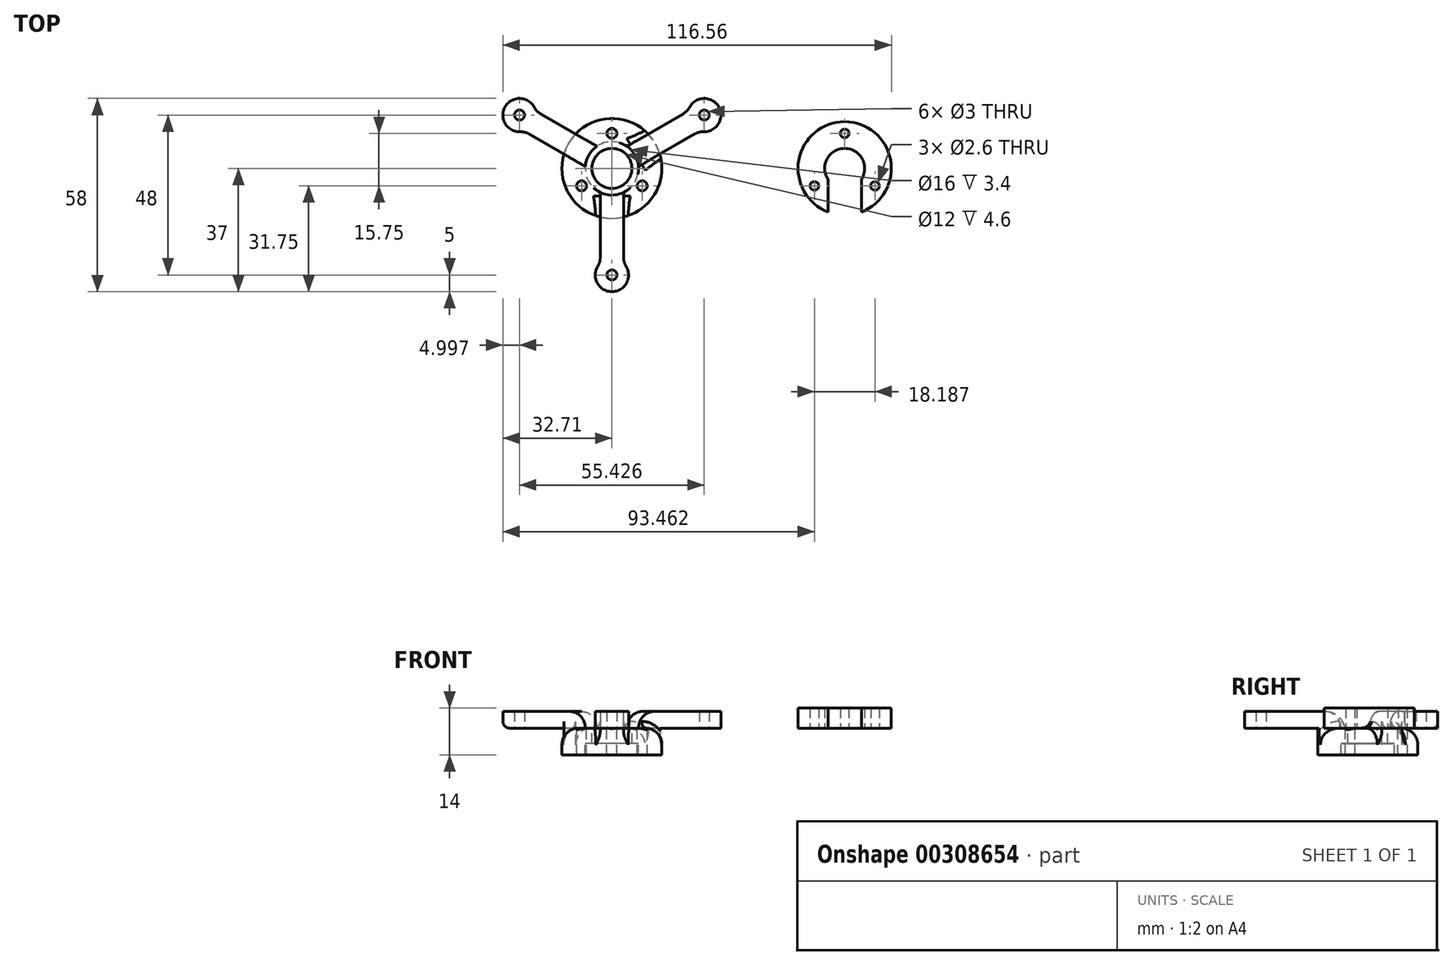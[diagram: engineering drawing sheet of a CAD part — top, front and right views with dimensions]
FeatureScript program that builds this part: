
annotation { "Feature Type Name" : "Feature", "Feature Type Description" : "" }
export const myFeature = defineFeature(function(context is Context, id is Id, definition is map)
    precondition{}
    {
        {
            var Q0;
            Q0=qCreatedBy(makeId("Top.planeOp"),FACE);
            var sketch = newSketch(context, id + "F0", { "sketchPlane" : qUnion([Q0])});
            skCircle(sketch, "E0", {"center": v(0, 0) * mm, "radius": 32 * mm});
            skLineSegment(sketch, "E1", {"start": v(5.2, 3) * mm, "end": v(27.71, 16) * mm});
            skCircle(sketch, "E2", {"center": v(27.71, 16) * mm, "radius": 1.5 * mm});
            skCircle(sketch, "E3", {"center": v(27.71, 16) * mm, "radius": 5 * mm});
            skLineSegment(sketch, "E4", {"start": v(25.11, 14.5) * mm, "end": v(23.36, 17.53) * mm});
            skLineSegment(sketch, "E5", {"start": v(23.36, 17.53) * mm, "end": v(20.33, 15.78) * mm});
            skLineSegment(sketch, "E6", {"start": v(20.33, 15.78) * mm, "end": v(22.08, 12.75) * mm});
            skLineSegment(sketch, "E7.MirrorCS", {"start": v(26.86, 11.47) * mm, "end": v(23.83, 9.72) * mm});
            skLineSegment(sketch, "E8.MirrorCS", {"start": v(23.83, 9.72) * mm, "end": v(22.08, 12.75) * mm});
            skLineSegment(sketch, "E9.MirrorCS", {"start": v(25.11, 14.5) * mm, "end": v(26.86, 11.47) * mm});
            skCircle(sketch, "E10.1.0", {"center": v(-27.71, 16) * mm, "radius": 5 * mm});
            skCircle(sketch, "E10.1.1", {"center": v(-27.71, 16) * mm, "radius": 1.5 * mm});
            skLineSegment(sketch, "E10.1.2", {"start": v(-25.11, 14.5) * mm, "end": v(-26.86, 11.47) * mm});
            skLineSegment(sketch, "E10.1.3", {"start": v(-25.11, 14.5) * mm, "end": v(-23.36, 17.53) * mm});
            skLineSegment(sketch, "E10.1.4", {"start": v(-23.36, 17.53) * mm, "end": v(-20.33, 15.78) * mm});
            skLineSegment(sketch, "E10.1.5", {"start": v(-20.33, 15.78) * mm, "end": v(-22.08, 12.75) * mm});
            skLineSegment(sketch, "E10.1.6", {"start": v(-23.83, 9.72) * mm, "end": v(-22.08, 12.75) * mm});
            skLineSegment(sketch, "E10.1.7", {"start": v(-26.86, 11.47) * mm, "end": v(-23.83, 9.72) * mm});
            skCircle(sketch, "E10.2.0", {"center": v(0, -32) * mm, "radius": 5 * mm});
            skCircle(sketch, "E10.2.1", {"center": v(0, -32) * mm, "radius": 1.5 * mm});
            skLineSegment(sketch, "E10.2.2", {"start": v(0, -29) * mm, "end": v(3.5, -29) * mm});
            skLineSegment(sketch, "E10.2.3", {"start": v(0, -29) * mm, "end": v(-3.5, -29) * mm});
            skLineSegment(sketch, "E10.2.4", {"start": v(-3.5, -29) * mm, "end": v(-3.5, -25.5) * mm});
            skLineSegment(sketch, "E10.2.5", {"start": v(-3.5, -25.5) * mm, "end": v(0, -25.5) * mm});
            skLineSegment(sketch, "E10.2.6", {"start": v(3.5, -25.5) * mm, "end": v(0, -25.5) * mm});
            skLineSegment(sketch, "E10.2.7", {"start": v(3.5, -29) * mm, "end": v(3.5, -25.5) * mm});
            skLineSegment(sketch, "E11.0", {"start": v(5.97, -0.6) * mm, "end": v(29.3, 12.87) * mm});
            skLineSegment(sketch, "E12.0", {"start": v(2.47, 5.47) * mm, "end": v(25.8, 18.94) * mm});
            skCircle(sketch, "E13", {"center": v(0, 0) * mm, "radius": 6 * mm});
            skCircle(sketch, "E14", {"center": v(0, 0) * mm, "radius": 8 * mm});
            skCircle(sketch, "E15", {"center": v(0, 0) * mm, "radius": 15 * mm});
            skLineSegment(sketch, "E16", {"start": v(-32.04, 13.5) * mm, "end": v(-4.33, -34.5) * mm});
            skLineSegment(sketch, "E17", {"start": v(-18.19, -10.5) * mm, "end": v(-16.45, -9.5) * mm});
            skCircle(sketch, "E18", {"center": v(0, 0) * mm, "radius": 25 * mm});
            skCircle(sketch, "E19", {"center": v(0, 10.5) * mm, "radius": 1.5 * mm});
            skCircle(sketch, "E20.1.0", {"center": v(-9.1, -5.25) * mm, "radius": 1.5 * mm});
            skCircle(sketch, "E20.2.0", {"center": v(9.1, -5.25) * mm, "radius": 1.5 * mm});
            skCircle(sketch, "E21", {"center": v(69.85, 0) * mm, "radius": 6 * mm});
            skCircle(sketch, "E22", {"center": v(69.85, 0) * mm, "radius": 14 * mm});
            skCircle(sketch, "E23", {"center": v(69.85, 10.5) * mm, "radius": 1.3 * mm});
            skCircle(sketch, "E24.1.0", {"center": v(60.75, -5.25) * mm, "radius": 1.3 * mm});
            skCircle(sketch, "E24.2.0", {"center": v(78.94, -5.25) * mm, "radius": 1.3 * mm});
            skLineSegment(sketch, "E25", {"start": v(69.85, -6) * mm, "end": v(69.85, -14) * mm});
            skLineSegment(sketch, "E26.0", {"start": v(64.85, -3.32) * mm, "end": v(64.85, -13.08) * mm});
            skLineSegment(sketch, "E27.0", {"start": v(74.85, -3.32) * mm, "end": v(74.85, -13.08) * mm});
            skSolve(sketch);
        }
        {
            var Q0;
            {var subQ0=sQuery(id+"F0.wireOp",EDGE,"E3");var subQ1=sQuery(id+"F0.wireOp",EDGE,"E0");var subQ2=makeQuery(id+"F0.imprint","INTERSECT",VERTEX,{"disambiguationData":[OD(0.0)],"derivedFrom":[subQ1,subQ0]});Q0=makeQuery(id+"F0.imprint","IMPRINT",FACE,{"disambiguationData":[TD([[makeQuery(id+"F0.imprint","IMPRINT",EDGE,{"disambiguationData":[TD([[subQ2,-1.0]])],"derivedFrom":subQ1}),-1.0]])]});}
            var Q1;
            {var subQ9=sQuery(id+"F0.wireOp",EDGE,"E4");Q1=makeQuery(id+"F0.imprint","IMPRINT",FACE,{"disambiguationData":[TD([[makeQuery(id+"F0.imprint","IMPRINT",EDGE,{"derivedFrom":subQ9}),-1.0]])]});}
            var Q2;
            {var subQ9=sQuery(id+"F0.wireOp",EDGE,"E9.MirrorCS");Q2=makeQuery(id+"F0.imprint","IMPRINT",FACE,{"disambiguationData":[TD([[makeQuery(id+"F0.imprint","IMPRINT",EDGE,{"derivedFrom":subQ9}),1.0]])]});}
            var Q3;
            {var subQ0=sQuery(id+"F0.wireOp",EDGE,"E9.MirrorCS");Q3=makeQuery(id+"F0.imprint","IMPRINT",FACE,{"disambiguationData":[TD([[makeQuery(id+"F0.imprint","IMPRINT",EDGE,{"derivedFrom":subQ0}),-1.0]])]});}
            var Q4;
            {var subQ0=sQuery(id+"F0.wireOp",EDGE,"E4");Q4=makeQuery(id+"F0.imprint","IMPRINT",FACE,{"disambiguationData":[TD([[makeQuery(id+"F0.imprint","IMPRINT",EDGE,{"derivedFrom":subQ0}),1.0]])]});}
            var Q5;
            {var subQ0=sQuery(id+"F0.wireOp",EDGE,"E11.0");var subQ1=sQuery(id+"F0.wireOp",EDGE,"E0");var subQ2=makeQuery(id+"F0.imprint","INTERSECT",VERTEX,{"derivedFrom":[subQ1,subQ0]});Q5=makeQuery(id+"F0.imprint","IMPRINT",FACE,{"disambiguationData":[TD([[makeQuery(id+"F0.imprint","IMPRINT",EDGE,{"disambiguationData":[TD([[subQ2,1.0]])],"derivedFrom":subQ1}),1.0]])]});}
            var Q6;
            {var subQ0=sQuery(id+"F0.wireOp",EDGE,"E12.0");var subQ1=sQuery(id+"F0.wireOp",EDGE,"E0");var subQ2=makeQuery(id+"F0.imprint","INTERSECT",VERTEX,{"derivedFrom":[subQ1,subQ0]});Q6=makeQuery(id+"F0.imprint","IMPRINT",FACE,{"disambiguationData":[TD([[makeQuery(id+"F0.imprint","IMPRINT",EDGE,{"disambiguationData":[TD([[subQ2,-1.0]])],"derivedFrom":subQ1}),1.0]])]});}
            extrude(context, id + "F1", {"entities" : qUnion([Q0, Q1, Q2, Q3, Q4, Q5, Q6]), "depth" : 5 * mm});
        }
        {
            var Q0;
            {var subQ0=sQuery(id+"F0.wireOp",EDGE,"E8.MirrorCS");Q0=makeQuery(id+"F0.imprint","IMPRINT",FACE,{"disambiguationData":[TD([[makeQuery(id+"F0.imprint","IMPRINT",EDGE,{"derivedFrom":subQ0}),-1.0]])]});}
            var Q1;
            {var subQ0=sQuery(id+"F0.wireOp",EDGE,"E6");Q1=makeQuery(id+"F0.imprint","IMPRINT",FACE,{"disambiguationData":[TD([[makeQuery(id+"F0.imprint","IMPRINT",EDGE,{"derivedFrom":subQ0}),1.0]])]});}
            var Q2;
            {var subQ0=sQuery(id+"F0.wireOp",EDGE,"E9.MirrorCS");Q2=makeQuery(id+"F0.imprint","IMPRINT",FACE,{"disambiguationData":[TD([[makeQuery(id+"F0.imprint","IMPRINT",EDGE,{"derivedFrom":subQ0}),-1.0]])]});}
            var Q3;
            {var subQ0=sQuery(id+"F0.wireOp",EDGE,"E4");Q3=makeQuery(id+"F0.imprint","IMPRINT",FACE,{"disambiguationData":[TD([[makeQuery(id+"F0.imprint","IMPRINT",EDGE,{"derivedFrom":subQ0}),1.0]])]});}
            var Q4;
            {var subQ0=sQuery(id+"F0.wireOp",EDGE,"E6");Q4=makeQuery(id+"F0.imprint","IMPRINT",FACE,{"disambiguationData":[TD([[makeQuery(id+"F0.imprint","IMPRINT",EDGE,{"derivedFrom":subQ0}),-1.0]])]});}
            var Q5;
            {var subQ0=sQuery(id+"F0.wireOp",EDGE,"E8.MirrorCS");Q5=makeQuery(id+"F0.imprint","IMPRINT",FACE,{"disambiguationData":[TD([[makeQuery(id+"F0.imprint","IMPRINT",EDGE,{"derivedFrom":subQ0}),1.0]])]});}
            var Q6;
            {var subQ0=sQuery(id+"F0.wireOp",EDGE,"E15");var subQ1=sQuery(id+"F0.wireOp",EDGE,"E1");var subQ2=makeQuery(id+"F0.imprint","INTERSECT",VERTEX,{"derivedFrom":[subQ1,subQ0]});Q6=makeQuery(id+"F0.imprint","IMPRINT",FACE,{"disambiguationData":[TD([[makeQuery(id+"F0.imprint","IMPRINT",EDGE,{"disambiguationData":[TD([[subQ2,-1.0]])],"derivedFrom":subQ1}),-1.0]])]});}
            var Q7;
            {var subQ0=sQuery(id+"F0.wireOp",EDGE,"E15");var subQ1=sQuery(id+"F0.wireOp",EDGE,"E1");var subQ2=makeQuery(id+"F0.imprint","INTERSECT",VERTEX,{"derivedFrom":[subQ1,subQ0]});Q7=makeQuery(id+"F0.imprint","IMPRINT",FACE,{"disambiguationData":[TD([[makeQuery(id+"F0.imprint","IMPRINT",EDGE,{"disambiguationData":[TD([[subQ2,-1.0]])],"derivedFrom":subQ1}),1.0]])]});}
            var Q8;
            {var subQ0=sQuery(id+"F0.wireOp",EDGE,"E14");var subQ1=sQuery(id+"F0.wireOp",EDGE,"E1");var subQ2=makeQuery(id+"F0.imprint","INTERSECT",VERTEX,{"derivedFrom":[subQ1,subQ0]});Q8=makeQuery(id+"F0.imprint","IMPRINT",FACE,{"disambiguationData":[TD([[makeQuery(id+"F0.imprint","IMPRINT",EDGE,{"disambiguationData":[TD([[subQ2,-1.0]])],"derivedFrom":subQ1}),1.0]])]});}
            var Q9;
            {var subQ0=sQuery(id+"F0.wireOp",EDGE,"E14");var subQ1=sQuery(id+"F0.wireOp",EDGE,"E1");var subQ2=makeQuery(id+"F0.imprint","INTERSECT",VERTEX,{"derivedFrom":[subQ1,subQ0]});Q9=makeQuery(id+"F0.imprint","IMPRINT",FACE,{"disambiguationData":[TD([[makeQuery(id+"F0.imprint","IMPRINT",EDGE,{"disambiguationData":[TD([[subQ2,-1.0]])],"derivedFrom":subQ1}),-1.0]])]});}
            extrude(context, id + "F2", {"entities" : qUnion([Q0, Q1, Q2, Q3, Q4, Q5, Q6, Q7, Q8, Q9]), "operationType" : NewBodyOperationType.ADD, "depth" : 5 * mm});
        }
        {
            var Q0;
            {var subQ0=sQuery(id+"F0.wireOp",EDGE,"E14");var subQ1=sQuery(id+"F0.wireOp",EDGE,"E1");var subQ2=makeQuery(id+"F0.imprint","INTERSECT",VERTEX,{"derivedFrom":[subQ1,subQ0]});Q0=makeQuery(id+"F0.imprint","IMPRINT",FACE,{"disambiguationData":[TD([[makeQuery(id+"F0.imprint","IMPRINT",EDGE,{"disambiguationData":[TD([[subQ2,-1.0]])],"derivedFrom":subQ1}),1.0]])]});}
            var Q1;
            {var subQ0=sQuery(id+"F0.wireOp",EDGE,"E14");var subQ1=sQuery(id+"F0.wireOp",EDGE,"E1");var subQ2=makeQuery(id+"F0.imprint","INTERSECT",VERTEX,{"derivedFrom":[subQ1,subQ0]});Q1=makeQuery(id+"F0.imprint","IMPRINT",FACE,{"disambiguationData":[TD([[makeQuery(id+"F0.imprint","IMPRINT",EDGE,{"disambiguationData":[TD([[subQ2,-1.0]])],"derivedFrom":subQ1}),-1.0]])]});}
            var Q2;
            {var subQ0=sQuery(id+"F0.wireOp",EDGE,"E14");var subQ1=sQuery(id+"F0.wireOp",EDGE,"E11.0");var subQ2=makeQuery(id+"F0.imprint","INTERSECT",VERTEX,{"derivedFrom":[subQ1,subQ0]});Q2=makeQuery(id+"F0.imprint","IMPRINT",FACE,{"disambiguationData":[TD([[makeQuery(id+"F0.imprint","IMPRINT",EDGE,{"disambiguationData":[TD([[subQ2,-1.0]])],"derivedFrom":subQ1}),-1.0]])]});}
            extrude(context, id + "F3", {"entities" : qUnion([Q0, Q1, Q2]), "oppositeDirection" : true, "depth" : 8 * mm});
        }
        {
            var Q0;
            Q0=makeQuery(id+"F1.opExtrude","SWEPT_BODY",BODY,{"disambiguationData":[OSD([sQuery(id+"F0.wireOp",EDGE,"E2"),sQuery(id+"F0.wireOp",EDGE,"E3")])]});
            var Q1;
            Q1=sQuery(id+"F0.wireOp",EDGE,"E0");
            circularPattern(context, id + "F4", {"entities" : qUnion([Q0]), "axis" : qUnion([Q1]), "angle" : 360 * degree, "instanceCount" : 3, "equalSpace" : true});
        }
        {
            var Q0;
            {var subQ0=sQuery(id+"F0.wireOp",EDGE,"E13");var subQ1=sQuery(id+"F0.wireOp",EDGE,"E11.0");var subQ2=makeQuery(id+"F0.imprint","INTERSECT",VERTEX,{"derivedFrom":[subQ1,subQ0]});Q0=makeQuery(id+"F0.imprint","IMPRINT",FACE,{"disambiguationData":[TD([[makeQuery(id+"F0.imprint","IMPRINT",EDGE,{"disambiguationData":[TD([[subQ2,-1.0]])],"derivedFrom":subQ1}),-1.0]])]});}
            var Q1;
            {var subQ0=sQuery(id+"F0.wireOp",EDGE,"E13");var subQ1=sQuery(id+"F0.wireOp",EDGE,"E1");var subQ2=makeQuery(id+"F0.imprint","INTERSECT",VERTEX,{"derivedFrom":[subQ1,subQ0]});Q1=makeQuery(id+"F0.imprint","IMPRINT",FACE,{"disambiguationData":[TD([[makeQuery(id+"F0.imprint","IMPRINT",EDGE,{"disambiguationData":[TD([[subQ2,-1.0]])],"derivedFrom":subQ1}),1.0]])]});}
            var Q2;
            {var subQ0=sQuery(id+"F0.wireOp",EDGE,"E13");var subQ1=sQuery(id+"F0.wireOp",EDGE,"E1");var subQ2=makeQuery(id+"F0.imprint","INTERSECT",VERTEX,{"derivedFrom":[subQ1,subQ0]});Q2=makeQuery(id+"F0.imprint","IMPRINT",FACE,{"disambiguationData":[TD([[makeQuery(id+"F0.imprint","IMPRINT",EDGE,{"disambiguationData":[TD([[subQ2,-1.0]])],"derivedFrom":subQ1}),-1.0]])]});}
            extrude(context, id + "F5", {"entities" : qUnion([Q0, Q1, Q2]), "oppositeDirection" : true, "depth" : 4.6 * mm});
        }
        {
            var Q0;
            Q0=makeQuery(id+"F4.opPattern","COPY",EDGE,{"derivedFrom":makeQuery(id+"F2.boolean.opBoolean","INTERSECT",EDGE,{"derivedFrom":[makeQuery(id+"F1.opExtrude","SWEPT_FACE",FACE,{"disambiguationData":[OSD([sQuery(id+"F0.wireOp",EDGE,"E3")])]}),makeQuery(id+"F2.opExtrude","SWEPT_FACE",FACE,{"disambiguationData":[OSD([sQuery(id+"F0.wireOp",EDGE,"E12.0")])]})]}),"instanceName":"2"});
            var Q1;
            Q1=makeQuery(id+"F4.opPattern","COPY",EDGE,{"derivedFrom":makeQuery(id+"F2.boolean.opBoolean","INTERSECT",EDGE,{"derivedFrom":[makeQuery(id+"F1.opExtrude","SWEPT_FACE",FACE,{"disambiguationData":[OSD([sQuery(id+"F0.wireOp",EDGE,"E3")])]}),makeQuery(id+"F2.opExtrude","SWEPT_FACE",FACE,{"disambiguationData":[OSD([sQuery(id+"F0.wireOp",EDGE,"E11.0")])]})]}),"instanceName":"2"});
            var Q2;
            Q2=makeQuery(id+"F2.boolean.opBoolean","INTERSECT",EDGE,{"derivedFrom":[makeQuery(id+"F1.opExtrude","SWEPT_FACE",FACE,{"disambiguationData":[OSD([sQuery(id+"F0.wireOp",EDGE,"E3")])]}),makeQuery(id+"F2.opExtrude","SWEPT_FACE",FACE,{"disambiguationData":[OSD([sQuery(id+"F0.wireOp",EDGE,"E11.0")])]})]});
            var Q3;
            Q3=makeQuery(id+"F2.boolean.opBoolean","INTERSECT",EDGE,{"derivedFrom":[makeQuery(id+"F1.opExtrude","SWEPT_FACE",FACE,{"disambiguationData":[OSD([sQuery(id+"F0.wireOp",EDGE,"E3")])]}),makeQuery(id+"F2.opExtrude","SWEPT_FACE",FACE,{"disambiguationData":[OSD([sQuery(id+"F0.wireOp",EDGE,"E12.0")])]})]});
            var Q4;
            Q4=makeQuery(id+"F4.opPattern","COPY",EDGE,{"derivedFrom":makeQuery(id+"F2.boolean.opBoolean","INTERSECT",EDGE,{"derivedFrom":[makeQuery(id+"F1.opExtrude","SWEPT_FACE",FACE,{"disambiguationData":[OSD([sQuery(id+"F0.wireOp",EDGE,"E3")])]}),makeQuery(id+"F2.opExtrude","SWEPT_FACE",FACE,{"disambiguationData":[OSD([sQuery(id+"F0.wireOp",EDGE,"E11.0")])]})]}),"instanceName":"1"});
            var Q5;
            Q5=makeQuery(id+"F4.opPattern","COPY",EDGE,{"derivedFrom":makeQuery(id+"F2.boolean.opBoolean","INTERSECT",EDGE,{"derivedFrom":[makeQuery(id+"F1.opExtrude","SWEPT_FACE",FACE,{"disambiguationData":[OSD([sQuery(id+"F0.wireOp",EDGE,"E3")])]}),makeQuery(id+"F2.opExtrude","SWEPT_FACE",FACE,{"disambiguationData":[OSD([sQuery(id+"F0.wireOp",EDGE,"E12.0")])]})]}),"instanceName":"1"});
            fillet(context, id + "F6", {"entities" : qUnion([Q0, Q1, Q2, Q3, Q4, Q5]), "radius" : 5 * mm, "tangentPropagation" : true, "allowEdgeOverflow" : false});
        }
        {
            var Q0;
            Q0=makeQuery(id+"F0.imprint","IMPRINT",FACE,{"disambiguationData":[TD([[makeQuery(id+"F0.imprint","IMPRINT",EDGE,{"derivedFrom":sQuery(id+"F0.wireOp",EDGE,"E23")}),-1.0]])]});
            extrude(context, id + "F7", {"entities" : qUnion([Q0]), "depth" : 6 * mm});
        }
        {
            var Q0;
            Q0=makeQuery(id+"F4.opPattern","COPY",BODY,{"derivedFrom":makeQuery(id+"F1.opExtrude","SWEPT_BODY",BODY,{"disambiguationData":[OSD([sQuery(id+"F0.wireOp",EDGE,"E2"),sQuery(id+"F0.wireOp",EDGE,"E3")])]}),"instanceName":"1"});
            var Q1;
            Q1=makeQuery(id+"F1.opExtrude","SWEPT_BODY",BODY,{"disambiguationData":[OSD([sQuery(id+"F0.wireOp",EDGE,"E2"),sQuery(id+"F0.wireOp",EDGE,"E3")])]});
            var Q2;
            Q2=makeQuery(id+"F4.opPattern","COPY",BODY,{"derivedFrom":makeQuery(id+"F1.opExtrude","SWEPT_BODY",BODY,{"disambiguationData":[OSD([sQuery(id+"F0.wireOp",EDGE,"E2"),sQuery(id+"F0.wireOp",EDGE,"E3")])]}),"instanceName":"2"});
            var Q3;
            Q3=makeQuery(id+"F3.opExtrude","SWEPT_BODY",BODY,{"disambiguationData":[OSD([sQuery(id+"F0.wireOp",EDGE,"E14"),sQuery(id+"F0.wireOp",EDGE,"E15"),sQuery(id+"F0.wireOp",EDGE,"E19"),sQuery(id+"F0.wireOp",EDGE,"E20.1.0"),sQuery(id+"F0.wireOp",EDGE,"E20.2.0")])]});
            var Q4;
            Q4=makeQuery(id+"F5.opExtrude","SWEPT_BODY",BODY,{"disambiguationData":[OSD([sQuery(id+"F0.wireOp",EDGE,"E13"),sQuery(id+"F0.wireOp",EDGE,"E14")])]});
            booleanBodies(context, id + "F8", {"operationType" : BooleanOperationType.UNION, "tools" : qUnion([Q0, Q1, Q2, Q3, Q4])});
        }
        {
            var Q0;
            Q0=makeQuery(id+"F4.opPattern","COPY",EDGE,{"derivedFrom":makeQuery(id+"F2.opExtrude","CAP_EDGE",EDGE,{"disambiguationData":[OSD([sQuery(id+"F0.wireOp",EDGE,"E14")])],"isStart":false}),"instanceName":"1"});
            var Q1;
            Q1=makeQuery(id+"F2.opExtrude","CAP_EDGE",EDGE,{"disambiguationData":[OSD([sQuery(id+"F0.wireOp",EDGE,"E14")])],"isStart":false});
            var Q2;
            Q2=makeQuery(id+"F4.opPattern","COPY",EDGE,{"derivedFrom":makeQuery(id+"F2.opExtrude","CAP_EDGE",EDGE,{"disambiguationData":[OSD([sQuery(id+"F0.wireOp",EDGE,"E14")])],"isStart":false}),"instanceName":"2"});
            fillet(context, id + "F9", {"entities" : qUnion([Q0, Q1, Q2]), "radius" : 5 * mm, "tangentPropagation" : true, "allowEdgeOverflow" : false});
        }
        {
            var Q0;
            {var subQ0=sQuery(id+"F0.wireOp",EDGE,"E15");Q0=makeQuery(id+"F8.opBoolean","SPLIT",EDGE,{"disambiguationData":[topologyDisambiguationEdgeConnected([makeQuery(id+"F1.opExtrude","CAP_FACE",FACE,{"disambiguationData":[OSD([sQuery(id+"F0.wireOp",EDGE,"E2"),sQuery(id+"F0.wireOp",EDGE,"E3")])],"isStart":true}),makeQuery(id+"F2.opExtrude","CAP_FACE",FACE,{"disambiguationData":[OSD([sQuery(id+"F0.wireOp",EDGE,"E4"),sQuery(id+"F0.wireOp",EDGE,"E9.MirrorCS"),sQuery(id+"F0.wireOp",EDGE,"E11.0"),sQuery(id+"F0.wireOp",EDGE,"E12.0"),sQuery(id+"F0.wireOp",EDGE,"E14")])],"isStart":true}),makeQuery(id+"F3.opExtrude","SWEPT_FACE",FACE,{"disambiguationData":[OSD([subQ0])]})])],"derivedFrom":makeQuery(id+"F3.opExtrude","CAP_EDGE",EDGE,{"disambiguationData":[OSD([subQ0])],"isStart":true})});}
            var Q1;
            {var subQ0=sQuery(id+"F0.wireOp",EDGE,"E15");Q1=makeQuery(id+"F8.opBoolean","SPLIT",EDGE,{"disambiguationData":[topologyDisambiguationEdgeConnected([makeQuery(id+"F3.opExtrude","SWEPT_FACE",FACE,{"disambiguationData":[OSD([subQ0])]}),makeQuery(id+"F4.opPattern","COPY",FACE,{"derivedFrom":makeQuery(id+"F2.boolean.opBoolean","MERGE",FACE,{"derivedFrom":[makeQuery(id+"F1.opExtrude","CAP_FACE",FACE,{"disambiguationData":[OSD([sQuery(id+"F0.wireOp",EDGE,"E2"),sQuery(id+"F0.wireOp",EDGE,"E3")])],"isStart":true}),makeQuery(id+"F2.opExtrude","CAP_FACE",FACE,{"disambiguationData":[OSD([sQuery(id+"F0.wireOp",EDGE,"E4"),sQuery(id+"F0.wireOp",EDGE,"E9.MirrorCS"),sQuery(id+"F0.wireOp",EDGE,"E11.0"),sQuery(id+"F0.wireOp",EDGE,"E12.0"),sQuery(id+"F0.wireOp",EDGE,"E14")])],"isStart":true})]}),"instanceName":"2"})])],"derivedFrom":makeQuery(id+"F3.opExtrude","CAP_EDGE",EDGE,{"disambiguationData":[OSD([subQ0])],"isStart":true})});}
            var Q2;
            {var subQ0=sQuery(id+"F0.wireOp",EDGE,"E15");Q2=makeQuery(id+"F8.opBoolean","SPLIT",EDGE,{"disambiguationData":[topologyDisambiguationEdgeConnected([makeQuery(id+"F3.opExtrude","SWEPT_FACE",FACE,{"disambiguationData":[OSD([subQ0])]}),makeQuery(id+"F4.opPattern","COPY",FACE,{"derivedFrom":makeQuery(id+"F2.boolean.opBoolean","MERGE",FACE,{"derivedFrom":[makeQuery(id+"F1.opExtrude","CAP_FACE",FACE,{"disambiguationData":[OSD([sQuery(id+"F0.wireOp",EDGE,"E2"),sQuery(id+"F0.wireOp",EDGE,"E3")])],"isStart":true}),makeQuery(id+"F2.opExtrude","CAP_FACE",FACE,{"disambiguationData":[OSD([sQuery(id+"F0.wireOp",EDGE,"E4"),sQuery(id+"F0.wireOp",EDGE,"E9.MirrorCS"),sQuery(id+"F0.wireOp",EDGE,"E11.0"),sQuery(id+"F0.wireOp",EDGE,"E12.0"),sQuery(id+"F0.wireOp",EDGE,"E14")])],"isStart":true})]}),"instanceName":"1"})])],"derivedFrom":makeQuery(id+"F3.opExtrude","CAP_EDGE",EDGE,{"disambiguationData":[OSD([subQ0])],"isStart":true})});}
            fillet(context, id + "F10", {"entities" : qUnion([Q0, Q1, Q2]), "radius" : 5 * mm, "tangentPropagation" : true, "allowEdgeOverflow" : false});
        }
        {
            var Q0;
            {var subQ0=sQuery(id+"F0.wireOp",EDGE,"E14");var subQ1=sQuery(id+"F0.wireOp",EDGE,"E11.0");Q0=makeQuery(id+"F8.opBoolean","SPLIT",EDGE,{"disambiguationData":[topologyDisambiguationEdgeConnected([makeQuery(id+"F5.opExtrude","CAP_FACE",FACE,{"disambiguationData":[OSD([sQuery(id+"F0.wireOp",EDGE,"E13"),subQ0])],"isStart":true})])],"derivedFrom":makeQuery(id+"F4.opPattern","COPY",EDGE,{"derivedFrom":makeQuery(id+"F2.opExtrude","CAP_EDGE",EDGE,{"disambiguationData":[OSD([subQ1])],"isStart":true}),"instanceName":"2"})});}
            var Q1;
            {var subQ0=sQuery(id+"F0.wireOp",EDGE,"E14");var subQ1=sQuery(id+"F0.wireOp",EDGE,"E12.0");Q1=makeQuery(id+"F8.opBoolean","SPLIT",EDGE,{"disambiguationData":[topologyDisambiguationEdgeConnected([makeQuery(id+"F5.opExtrude","CAP_FACE",FACE,{"disambiguationData":[OSD([sQuery(id+"F0.wireOp",EDGE,"E13"),subQ0])],"isStart":true})])],"derivedFrom":makeQuery(id+"F4.opPattern","COPY",EDGE,{"derivedFrom":makeQuery(id+"F2.opExtrude","CAP_EDGE",EDGE,{"disambiguationData":[OSD([subQ1])],"isStart":true}),"instanceName":"2"})});}
            var Q2;
            {var subQ0=sQuery(id+"F0.wireOp",EDGE,"E14");var subQ1=sQuery(id+"F0.wireOp",EDGE,"E12.0");Q2=makeQuery(id+"F8.opBoolean","SPLIT",EDGE,{"disambiguationData":[topologyDisambiguationEdgeConnected([makeQuery(id+"F5.opExtrude","CAP_FACE",FACE,{"disambiguationData":[OSD([sQuery(id+"F0.wireOp",EDGE,"E13"),subQ0])],"isStart":true})])],"derivedFrom":makeQuery(id+"F4.opPattern","COPY",EDGE,{"derivedFrom":makeQuery(id+"F2.opExtrude","CAP_EDGE",EDGE,{"disambiguationData":[OSD([subQ1])],"isStart":true}),"instanceName":"1"})});}
            var Q3;
            {var subQ0=sQuery(id+"F0.wireOp",EDGE,"E14");var subQ1=sQuery(id+"F0.wireOp",EDGE,"E11.0");Q3=makeQuery(id+"F8.opBoolean","SPLIT",EDGE,{"disambiguationData":[topologyDisambiguationEdgeConnected([makeQuery(id+"F5.opExtrude","CAP_FACE",FACE,{"disambiguationData":[OSD([sQuery(id+"F0.wireOp",EDGE,"E13"),subQ0])],"isStart":true})])],"derivedFrom":makeQuery(id+"F4.opPattern","COPY",EDGE,{"derivedFrom":makeQuery(id+"F2.opExtrude","CAP_EDGE",EDGE,{"disambiguationData":[OSD([subQ1])],"isStart":true}),"instanceName":"1"})});}
            var Q4;
            {var subQ0=sQuery(id+"F0.wireOp",EDGE,"E12.0");var subQ1=sQuery(id+"F0.wireOp",EDGE,"E14");Q4=makeQuery(id+"F8.opBoolean","SPLIT",EDGE,{"disambiguationData":[topologyDisambiguationEdgeConnected([makeQuery(id+"F5.opExtrude","CAP_FACE",FACE,{"disambiguationData":[OSD([sQuery(id+"F0.wireOp",EDGE,"E13"),subQ1])],"isStart":true})])],"derivedFrom":makeQuery(id+"F2.opExtrude","CAP_EDGE",EDGE,{"disambiguationData":[OSD([subQ0])],"isStart":true})});}
            var Q5;
            {var subQ0=sQuery(id+"F0.wireOp",EDGE,"E11.0");var subQ1=sQuery(id+"F0.wireOp",EDGE,"E14");Q5=makeQuery(id+"F8.opBoolean","SPLIT",EDGE,{"disambiguationData":[topologyDisambiguationEdgeConnected([makeQuery(id+"F5.opExtrude","CAP_FACE",FACE,{"disambiguationData":[OSD([sQuery(id+"F0.wireOp",EDGE,"E13"),subQ1])],"isStart":true})])],"derivedFrom":makeQuery(id+"F2.opExtrude","CAP_EDGE",EDGE,{"disambiguationData":[OSD([subQ0])],"isStart":true})});}
            fillet(context, id + "F11", {"entities" : qUnion([Q0, Q1, Q2, Q3, Q4, Q5]), "radius" : 2 * mm, "tangentPropagation" : true, "allowEdgeOverflow" : false});
        }
    });
